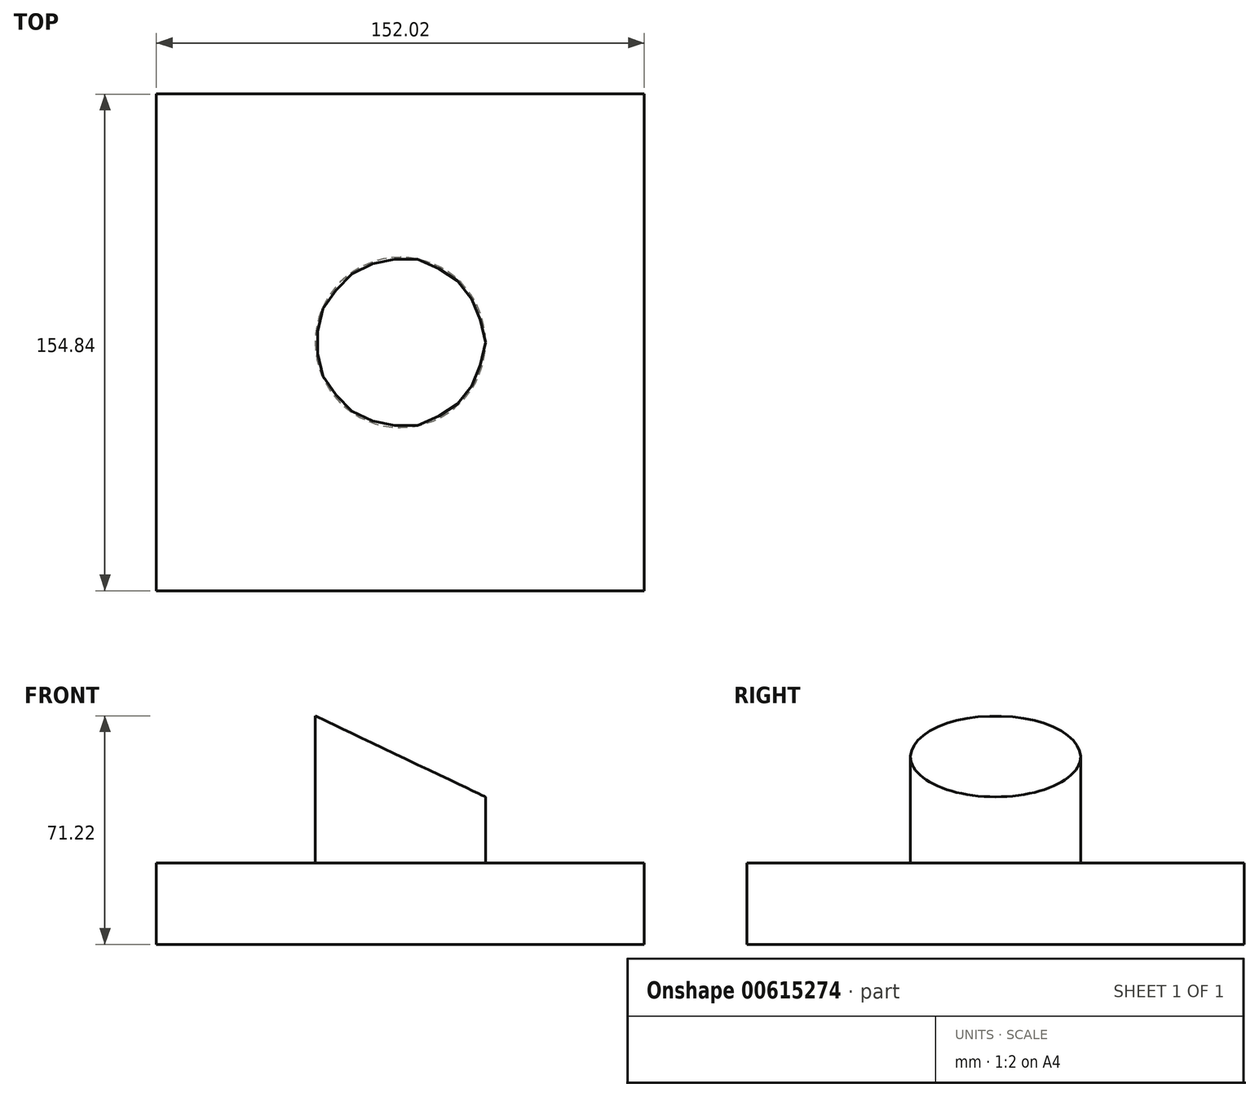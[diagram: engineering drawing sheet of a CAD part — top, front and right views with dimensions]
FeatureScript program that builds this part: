
annotation { "Feature Type Name" : "Feature", "Feature Type Description" : "" }
export const myFeature = defineFeature(function(context is Context, id is Id, definition is map)
    precondition{}
    {
        {
            var Q0;
            Q0=qCreatedBy(makeId("Top.planeOp"),FACE);
            var sketch = newSketch(context, id + "F0", { "sketchPlane" : qUnion([Q0])});
            skLineSegment(sketch, "E0.bottom", {"start": v(-76.01, 77.42) * mm, "end": v(76.01, 77.42) * mm});
            skLineSegment(sketch, "E0.top", {"start": v(-76.01, -77.42) * mm, "end": v(76.01, -77.42) * mm});
            skLineSegment(sketch, "E0.left", {"start": v(-76.01, 77.42) * mm, "end": v(-76.01, -77.42) * mm});
            skLineSegment(sketch, "E0.right", {"start": v(76.01, 77.42) * mm, "end": v(76.01, -77.42) * mm});
            skPoint(sketch, "E0.middle", {"position": v(0, 0) * mm});
            skSolve(sketch);
        }
        {
            var Q0;
            Q0 = qSketchRegion(id + "F0", true);
            extrude(context, id + "F1", {"entities" : qUnion([Q0]), "depth" : 25.4 * mm, "offsetDistance" : 25.4 * mm});
        }
        {
            var Q0;
            Q0=makeQuery(id+"F1.opExtrude","CAP_FACE",FACE,{"disambiguationData":[OSD([sQuery(id+"F0.wireOp",EDGE,"E0.bottom"),sQuery(id+"F0.wireOp",EDGE,"E0.top"),sQuery(id+"F0.wireOp",EDGE,"E0.left"),sQuery(id+"F0.wireOp",EDGE,"E0.right")])],"isStart":false});
            var sketch = newSketch(context, id + "F2", { "sketchPlane" : qUnion([Q0])});
            skCircle(sketch, "E1", {"center": v(0, 0) * mm, "radius": 26.53 * mm});
            skSolve(sketch);
        }
        {
            var Q0;
            Q0=makeQuery(id+"F2.imprint","IMPRINT",FACE,{"disambiguationData":[TD([[makeQuery(id+"F2.imprint","IMPRINT",EDGE,{"derivedFrom":sQuery(id+"F2.wireOp",EDGE,"E1")}),1.0]])]});
            extrude(context, id + "F3", {"entities" : qUnion([Q0]), "operationType" : NewBodyOperationType.ADD, "depth" : 50.8 * mm, "offsetDistance" : 25.4 * mm});
        }
        {
            var Q0;
            Q0=qCreatedBy(makeId("Front.planeOp"),FACE);
            var sketch = newSketch(context, id + "F4", { "sketchPlane" : qUnion([Q0])});
            skLineSegment(sketch, "E2", {"start": v(-37.48, 76.44) * mm, "end": v(36.02, 76.44) * mm});
            skLineSegment(sketch, "E3", {"start": v(36.02, 76.44) * mm, "end": v(36.02, 41.43) * mm});
            skLineSegment(sketch, "E4", {"start": v(36.02, 41.43) * mm, "end": v(-37.48, 76.44) * mm});
            skSolve(sketch);
        }
        {
            var Q0;
            Q0=makeQuery(id+"F4.imprint","IMPRINT",FACE,{"disambiguationData":[TD([[makeQuery(id+"F4.imprint","IMPRINT",EDGE,{"derivedFrom":sQuery(id+"F4.wireOp",EDGE,"E2")}),-1.0]])]});
            extrude(context, id + "F5", {"entities" : qUnion([Q0]), "operationType" : NewBodyOperationType.REMOVE, "endBound" : BoundingType.SYMMETRIC, "oppositeDirection" : true, "depth" : 508 * mm, "offsetDistance" : 25.4 * mm});
        }
    });
